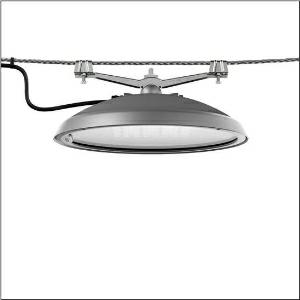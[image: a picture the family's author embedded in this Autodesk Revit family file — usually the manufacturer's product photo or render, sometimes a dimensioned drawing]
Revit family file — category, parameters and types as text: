
# Revit family: dl_r__50_iq_mini___st0_8s_5xa248v31f08ge_778c
name_source: partatom
category: Lighting Fixtures
units: mm (PartAtom-declared; Revit-internal decimal feet)

## family parameters
Cut with Voids When Loaded = No
Host = Face
Light Source = No
Part Type = Normal
Room Calculation Point = No
Round Connector Dimension = Use Diameter
Shared = No

## types (1)
- --- (1 x LED, 5190 lm, 32.7 W, 3000K)
    Apparent Load = 33 VA
    CIE Flux Codes = 38 75 97 100 100
    Color Rendering = 70
    Color Temperature = 3000K
    Default Elevation = 1800 mm
    Description = DL® 50 iQ mini, catenary luminaire, primary light control with lens, of PMMA, primary optical cover: cover, of toughened safety glass, transparent, light distribution: ST0.8s, light emission: direct distribution, primary light characteristic: symmetric, installation type: suspended mounting, LED, High Power LED, rated luminous flux: 5.190lm, luminous efficacy: 159lm/W, light colour: 730, colour temperature: 3000K, control gear: iQ Street-Remote, control: optimised constant luminous flux control (CLO 2.0), Desk-Remote (wireless, voltage-free reading and setting of iQ features in the workshop via application-optimized NFC function/RFID function), Light-Fading, Smart-Wire, Night-Set, Lumen-Switch, Temp-Guard, Auto-Match, Street-Remote, mains connection: 230..240V, AC, 50/60Hz, start of lifetime: 33W, end of service life: 34W, reduction: 16W, luminaire housing, of diecast aluminium, powder-coated, Siteco® metallic grey (DB 702S), diameter: 500mm, height: 115mm, mounting height: 4..12m, protection rating (complete): IP66, insulation class (complete): insulation class II (safety insulation), certification: CE, ENEC, ENEC+, VDE, impact resistance: IK08, permissible operating ambient temperature for outdoor applications: -25..+40°C, standard-compliant lighting for roads and squares, packaging unit: 1 piece

Light Distribution: ST0.8s
    Height = 124 mm
    Lamp = 1 x LED
    Lamp Light Flux = 5190 lm
    Lamp Power = 32.7 W
    Lamp count = 1
    Length = 500 mm
    Luminous efficacy = 159 lm/W
    Manufacturer = Siteco
    ModVariant = No
    Model = 5XA248V31F08GE
    Number of Poles = 1
    OnlyDefault = Yes
    Power Factor = 1
    Product Name = DL® 50 iQ mini | ST0.8s
    Product group = catenary luminaire
    ProductGroupID = 6300
    Protection Class = Protection class II
    Protection Degree = IP 66
    RLX_Detail_Level = 1
    RLX_Emergency_Light_Flux = 0 lm
    RLX_Emergency_Type = 0
    RLX_Emergency_Type_DB = No
    RlxData = <blob elided: 123625 chars, md5=2cad5c1c>
    Socket = socket
    Standby Power = 0 W
    System Light Flux = 5190 lm
    System Power = 33 W
    Type Comments = factory setting: luminous flux: 100 % | dim-lin: 254 | 340 mA
    Type Image = l_1242791.jpg
    URL = http://relux.com
    VarID = @adj_141134
    Voltage = 0 V
    Weight = 0.00 kg
    Width = 0 mm  [stored 0 ft]

note: [stored X ft] marks values corroborated as IEEE doubles in the binary element streams (Revit-internal decimal feet)

## geometry (parser evidence)
native form markers: Blend x4, Sweep x12
no freeform markers — native parametric forms only
